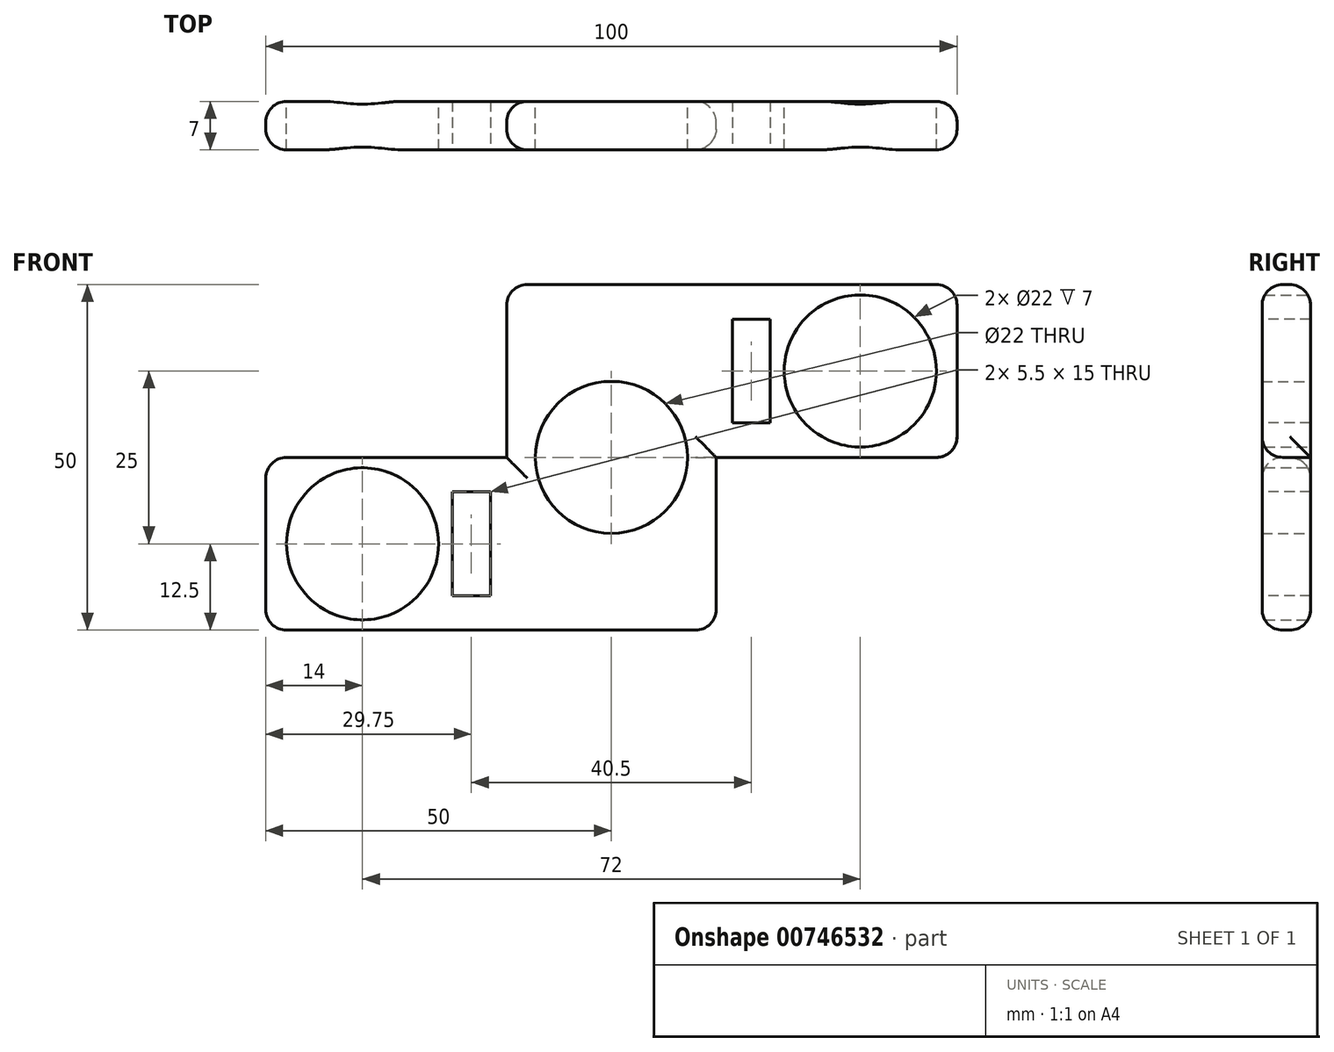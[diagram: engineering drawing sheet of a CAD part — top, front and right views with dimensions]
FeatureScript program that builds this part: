
annotation { "Feature Type Name" : "Feature", "Feature Type Description" : "" }
export const myFeature = defineFeature(function(context is Context, id is Id, definition is map)
    precondition{}
    {
        {
            var Q0;
            Q0=qCreatedBy(makeId("Front.planeOp"),FACE);
            var sketch = newSketch(context, id + "F0", { "sketchPlane" : qUnion([Q0])});
            skCircle(sketch, "E0", {"center": v(0, 0) * mm, "radius": 11 * mm});
            skSolve(sketch);
        }
        {
            var Q0;
            Q0=qCreatedBy(makeId("Front.planeOp"),FACE);
            var sketch = newSketch(context, id + "F1", { "sketchPlane" : qUnion([Q0])});
            skLineSegment(sketch, "E1.bottom", {"start": v(-50, 25) * mm, "end": v(50, 25) * mm});
            skLineSegment(sketch, "E1.top", {"start": v(-50, -25) * mm, "end": v(50, -25) * mm});
            skLineSegment(sketch, "E1.left", {"start": v(-50, 25) * mm, "end": v(-50, -25) * mm});
            skLineSegment(sketch, "E1.right", {"start": v(50, 25) * mm, "end": v(50, -25) * mm});
            skLineSegment(sketch, "E2.bottom", {"start": v(-50, 25) * mm, "end": v(-15.16, 25) * mm});
            skLineSegment(sketch, "E2.top", {"start": v(-50, 0) * mm, "end": v(-15.16, 0) * mm});
            skLineSegment(sketch, "E2.left", {"start": v(-50, 25) * mm, "end": v(-50, 0) * mm});
            skLineSegment(sketch, "E2.right", {"start": v(-15.16, 25) * mm, "end": v(-15.16, 0) * mm});
            skLineSegment(sketch, "E3.bottom", {"start": v(50, -25) * mm, "end": v(15.16, -25) * mm});
            skLineSegment(sketch, "E3.top", {"start": v(50, 0) * mm, "end": v(15.16, 0) * mm});
            skLineSegment(sketch, "E3.left", {"start": v(50, -25) * mm, "end": v(50, 0) * mm});
            skLineSegment(sketch, "E3.right", {"start": v(15.16, -25) * mm, "end": v(15.16, 0) * mm});
            skSolve(sketch);
        }
        {
            var Q0;
            {var subQ7=sQuery(id+"F1.wireOp",EDGE,"E2.top");Q0=makeQuery(id+"F1.imprint","IMPRINT",FACE,{"disambiguationData":[TD([[makeQuery(id+"F1.imprint","IMPRINT",EDGE,{"derivedFrom":subQ7}),-1.0]])]});}
            extrude(context, id + "F2", {"entities" : qUnion([Q0]), "depth" : 7 * mm, "offsetDistance" : 25 * mm});
        }
        {
            var Q0;
            Q0=qSketchRegion(id+"F0",true);
            extrude(context, id + "F3", {"entities" : qUnion([Q0]), "operationType" : NewBodyOperationType.REMOVE, "endBound" : BoundingType.THROUGH_ALL, "depth" : 25 * mm, "offsetDistance" : 25 * mm});
        }
        {
            var Q0;
            Q0=qCreatedBy(makeId("Front.planeOp"),FACE);
            var sketch = newSketch(context, id + "F4", { "sketchPlane" : qUnion([Q0])});
            skCircle(sketch, "E4", {"center": v(-36, -12.5) * mm, "radius": 11 * mm});
            skCircle(sketch, "E5", {"center": v(36, 12.5) * mm, "radius": 11 * mm});
            skSolve(sketch);
        }
        {
            var Q0;
            Q0=qSketchRegion(id+"F4",true);
            extrude(context, id + "F5", {"entities" : qUnion([Q0]), "operationType" : NewBodyOperationType.REMOVE, "endBound" : BoundingType.THROUGH_ALL, "depth" : 25 * mm, "offsetDistance" : 25 * mm});
        }
        {
            var Q0;
            Q0=makeQuery(id+"F2.opExtrude","CAP_EDGE",EDGE,{"disambiguationData":[OSD([sQuery(id+"F1.wireOp",EDGE,"E2.top")])],"isStart":false});
            var Q1;
            Q1=makeQuery(id+"F2.opExtrude","CAP_EDGE",EDGE,{"disambiguationData":[OSD([sQuery(id+"F1.wireOp",EDGE,"E2.top")])],"isStart":true});
            fillet(context, id + "F6", {"entities" : qUnion([Q0, Q1]), "radius" : 3 * mm, "tangentPropagation" : true, "allowEdgeOverflow" : false});
        }
        {
            var Q0;
            Q0=makeQuery(id+"F2.opExtrude","CAP_EDGE",EDGE,{"disambiguationData":[OSD([sQuery(id+"F1.wireOp",EDGE,"E1.top")])],"isStart":false});
            var Q1;
            Q1=makeQuery(id+"F2.opExtrude","CAP_EDGE",EDGE,{"disambiguationData":[OSD([sQuery(id+"F1.wireOp",EDGE,"E1.top")])],"isStart":true});
            fillet(context, id + "F7", {"entities" : qUnion([Q0, Q1]), "radius" : 3 * mm, "tangentPropagation" : true, "allowEdgeOverflow" : false});
        }
        {
            var Q0;
            Q0=makeQuery(id+"F2.opExtrude","CAP_EDGE",EDGE,{"disambiguationData":[OSD([sQuery(id+"F1.wireOp",EDGE,"E2.right")])],"isStart":false});
            var Q1;
            Q1=makeQuery(id+"F2.opExtrude","CAP_EDGE",EDGE,{"disambiguationData":[OSD([sQuery(id+"F1.wireOp",EDGE,"E2.right")])],"isStart":true});
            fillet(context, id + "F8", {"entities" : qUnion([Q0, Q1]), "radius" : 3 * mm, "tangentPropagation" : true, "allowEdgeOverflow" : false});
        }
        {
            var Q0;
            Q0=makeQuery(id+"F2.opExtrude","CAP_EDGE",EDGE,{"disambiguationData":[OSD([sQuery(id+"F1.wireOp",EDGE,"E3.right")])],"isStart":false});
            var Q1;
            Q1=makeQuery(id+"F2.opExtrude","CAP_EDGE",EDGE,{"disambiguationData":[OSD([sQuery(id+"F1.wireOp",EDGE,"E3.right")])],"isStart":true});
            fillet(context, id + "F9", {"entities" : qUnion([Q0, Q1]), "radius" : 3 * mm, "tangentPropagation" : true, "allowEdgeOverflow" : false});
        }
        {
            var Q0;
            Q0=makeQuery(id+"F2.opExtrude","CAP_EDGE",EDGE,{"disambiguationData":[OSD([sQuery(id+"F1.wireOp",EDGE,"E3.top")])],"isStart":false});
            fillet(context, id + "F10", {"entities" : qUnion([Q0]), "radius" : 3 * mm, "tangentPropagation" : true, "allowEdgeOverflow" : false});
        }
        {
            var Q0;
            Q0=makeQuery(id+"F2.opExtrude","CAP_EDGE",EDGE,{"disambiguationData":[OSD([sQuery(id+"F1.wireOp",EDGE,"E1.bottom")])],"isStart":false});
            var Q1;
            Q1=makeQuery(id+"F2.opExtrude","CAP_EDGE",EDGE,{"disambiguationData":[OSD([sQuery(id+"F1.wireOp",EDGE,"E1.bottom")])],"isStart":true});
            fillet(context, id + "F11", {"entities" : qUnion([Q0, Q1]), "radius" : 3 * mm, "tangentPropagation" : true, "allowEdgeOverflow" : false});
        }
        {
            var Q0;
            Q0=makeQuery(id+"F2.opExtrude","CAP_EDGE",EDGE,{"disambiguationData":[OSD([sQuery(id+"F1.wireOp",EDGE,"E1.right")])],"isStart":false});
            var Q1;
            Q1=makeQuery(id+"F2.opExtrude","SWEPT_FACE",FACE,{"disambiguationData":[OSD([sQuery(id+"F1.wireOp",EDGE,"E1.right")])]});
            fillet(context, id + "F12", {"entities" : qUnion([Q0, Q1]), "radius" : 3 * mm, "tangentPropagation" : true, "allowEdgeOverflow" : false});
        }
        {
            var Q0;
            Q0=makeQuery(id+"F2.opExtrude","SWEPT_FACE",FACE,{"disambiguationData":[OSD([sQuery(id+"F1.wireOp",EDGE,"E1.left")])]});
            fillet(context, id + "F13", {"entities" : qUnion([Q0]), "radius" : 3 * mm, "tangentPropagation" : true, "allowEdgeOverflow" : false});
        }
        {
            var Q0;
            Q0=makeQuery(id+"F11.opFillet","SPLIT",FACE,{"disambiguationData":[OD(0.0)],"derivedFrom":makeQuery(id+"F7.opFillet","SPLIT",FACE,{"disambiguationData":[OD(0.0)],"derivedFrom":makeQuery(id+"F2.opExtrude","CAP_FACE",FACE,{"disambiguationData":[OSD([sQuery(id+"F1.wireOp",EDGE,"E1.bottom"),sQuery(id+"F1.wireOp",EDGE,"E1.top"),sQuery(id+"F1.wireOp",EDGE,"E1.left"),sQuery(id+"F1.wireOp",EDGE,"E1.right"),sQuery(id+"F1.wireOp",EDGE,"E2.top"),sQuery(id+"F1.wireOp",EDGE,"E2.right"),sQuery(id+"F1.wireOp",EDGE,"E3.top"),sQuery(id+"F1.wireOp",EDGE,"E3.right")])],"isStart":false})})});
            var sketch = newSketch(context, id + "F14", { "sketchPlane" : qUnion([Q0])});
            skLineSegment(sketch, "E6.bottom", {"start": v(23, 5) * mm, "end": v(17.5, 5) * mm});
            skLineSegment(sketch, "E6.top", {"start": v(23, 20) * mm, "end": v(17.5, 20) * mm});
            skLineSegment(sketch, "E6.left", {"start": v(23, 5) * mm, "end": v(23, 20) * mm});
            skLineSegment(sketch, "E6.right", {"start": v(17.5, 5) * mm, "end": v(17.5, 20) * mm});
            skSolve(sketch);
        }
        {
            var Q0;
            Q0=makeQuery(id+"F14.imprint","IMPRINT",FACE,{"disambiguationData":[TD([[makeQuery(id+"F14.imprint","IMPRINT",EDGE,{"derivedFrom":sQuery(id+"F14.wireOp",EDGE,"E6.bottom")}),1.0]])]});
            var sketch = newSketch(context, id + "F15", { "sketchPlane" : qUnion([Q0])});
            skLineSegment(sketch, "E7.bottom", {"start": v(-23, -20) * mm, "end": v(-17.5, -20) * mm});
            skLineSegment(sketch, "E7.top", {"start": v(-23, -5) * mm, "end": v(-17.5, -5) * mm});
            skLineSegment(sketch, "E7.left", {"start": v(-23, -20) * mm, "end": v(-23, -5) * mm});
            skLineSegment(sketch, "E7.right", {"start": v(-17.5, -20) * mm, "end": v(-17.5, -5) * mm});
            skSolve(sketch);
        }
        {
            var Q0;
            Q0=qSketchRegion(id+"F15",true);
            extrude(context, id + "F16", {"entities" : qUnion([Q0]), "operationType" : NewBodyOperationType.REMOVE, "endBound" : BoundingType.THROUGH_ALL, "oppositeDirection" : true, "depth" : 25 * mm, "offsetDistance" : 25 * mm});
        }
        {
            var Q0;
            Q0=qSketchRegion(id+"F14",true);
            extrude(context, id + "F17", {"entities" : qUnion([Q0]), "operationType" : NewBodyOperationType.REMOVE, "endBound" : BoundingType.THROUGH_ALL, "oppositeDirection" : true, "depth" : 25 * mm, "offsetDistance" : 25 * mm});
        }
    });
